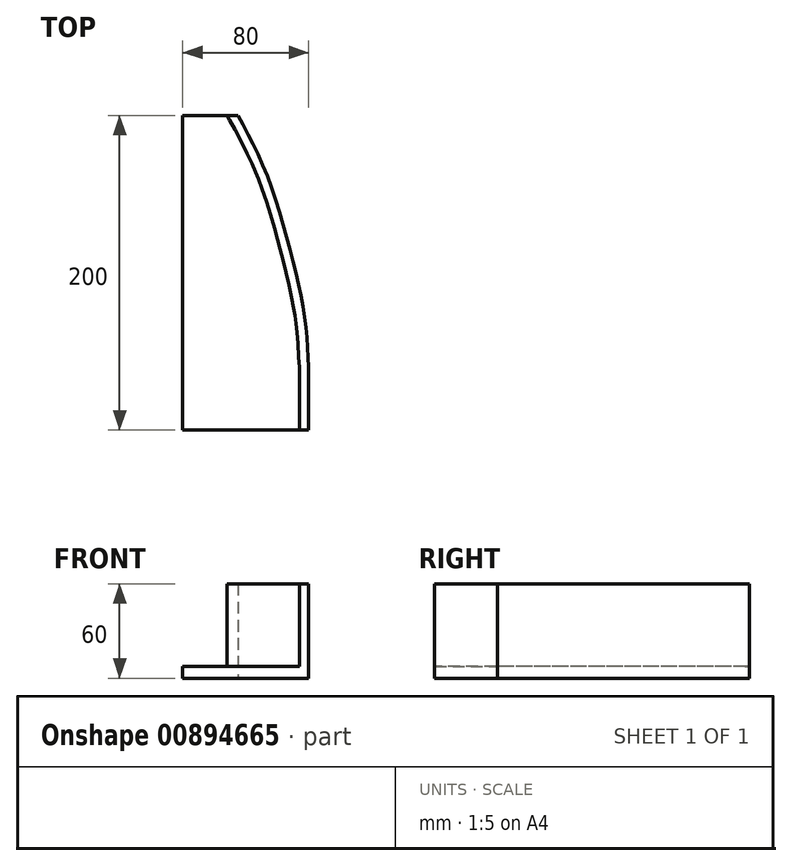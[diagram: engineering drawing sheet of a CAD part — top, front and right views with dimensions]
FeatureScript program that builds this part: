
annotation { "Feature Type Name" : "Feature", "Feature Type Description" : "" }
export const myFeature = defineFeature(function(context is Context, id is Id, definition is map)
    precondition{}
    {
        {
            var Q0;
            Q0=qCreatedBy(makeId("Top.planeOp"),FACE);
            var sketch = newSketch(context, id + "F0", { "sketchPlane" : qUnion([Q0])});
            skLineSegment(sketch, "E0.bottom", {"start": v(-38.43, 127.35) * mm, "end": v(41.57, 127.35) * mm});
            skLineSegment(sketch, "E0.top", {"start": v(-38.43, -72.65) * mm, "end": v(41.57, -72.65) * mm});
            skLineSegment(sketch, "E0.left", {"start": v(-38.43, 127.35) * mm, "end": v(-38.43, -72.65) * mm});
            skLineSegment(sketch, "E0.right", {"start": v(41.57, 127.35) * mm, "end": v(41.57, -72.65) * mm});
            skLineSegment(sketch, "E1", {"start": v(-38.43, 127.35) * mm, "end": v(-3.43, 127.35) * mm});
            skLineSegment(sketch, "E2", {"start": v(41.57, -72.65) * mm, "end": v(41.57, -32.65) * mm});
            skFitSpline(sketch, "E3", {"points": [v(-3.43, 127.35) * mm, v(14.22, 91.46) * mm, v(29.84, 41.68) * mm, v(38.82, 0) * mm, v(41.57, -32.65) * mm], "startDerivative": vector(75.12, -137.9) * mm, "endDerivative": vector(7.6, -144.15) * mm});
            skFitSpline(sketch, "E4.0", {"points": [v(-8.7, 124.48) * mm, v(-7.14, 121.6) * mm, v(-4.8, 117.32) * mm, v(-1.75, 111.54) * mm, v(0.5, 107.15) * mm, v(2.71, 102.68) * mm, v(4.5, 98.86) * mm, v(5.9, 95.73) * mm, v(6.95, 93.34) * mm, v(7.8, 91.32) * mm, v(8.47, 89.68) * mm, v(9.13, 88.03) * mm, v(9.96, 85.92) * mm, v(11.25, 82.49) * mm, v(12.83, 78.08) * mm, v(14.66, 72.65) * mm, v(16.43, 67.11) * mm, v(18.13, 61.5) * mm, v(19.78, 55.86) * mm, v(21.1, 51.15) * mm, v(22.11, 47.4) * mm, v(22.86, 44.6) * mm, v(23.6, 41.83) * mm, v(24.56, 38.15) * mm, v(25.72, 33.63) * mm, v(27.04, 28.32) * mm, v(28.27, 23.11) * mm, v(29.42, 18.02) * mm, v(30.47, 13.03) * mm, v(31.26, 8.96) * mm, v(31.84, 5.75) * mm, v(32.24, 3.37) * mm, v(32.55, 1.4) * mm, v(32.78, -0.15) * mm, v(33, -1.7) * mm, v(33.26, -3.63) * mm, v(33.55, -5.93) * mm, v(33.8, -8.21) * mm, v(34.12, -11.24) * mm, v(34.46, -15.01) * mm, v(34.8, -19.5) * mm, v(35.18, -25.48) * mm, v(35.42, -29.96) * mm, v(35.58, -32.97) * mm]});
            skLineSegment(sketch, "E5", {"start": v(35.58, -72.65) * mm, "end": v(35.58, -32.97) * mm});
            skLineSegment(sketch, "E6", {"start": v(-8.7, 124.48) * mm, "end": v(-10.25, 127.35) * mm});
            skSolve(sketch);
        }
        {
            var Q0;
            {var subQ0=sQuery(id+"F0.wireOp",EDGE,"E3");Q0=makeQuery(id+"F0.imprint","IMPRINT",FACE,{"disambiguationData":[TD([[makeQuery(id+"F0.imprint","IMPRINT",EDGE,{"derivedFrom":subQ0}),-1.0]])]});}
            extrude(context, id + "F1", {"entities" : qUnion([Q0]), "depth" : 60 * mm, "offsetDistance" : 25 * mm});
        }
        {
            var Q0;
            {var subQ0=sQuery(id+"F0.wireOp",EDGE,"E0.left");Q0=makeQuery(id+"F0.imprint","IMPRINT",FACE,{"disambiguationData":[TD([[makeQuery(id+"F0.imprint","IMPRINT",EDGE,{"derivedFrom":subQ0}),1.0]])]});}
            extrude(context, id + "F2", {"entities" : qUnion([Q0]), "operationType" : NewBodyOperationType.ADD, "depth" : 7.5 * mm, "offsetDistance" : 25 * mm});
        }
    });
